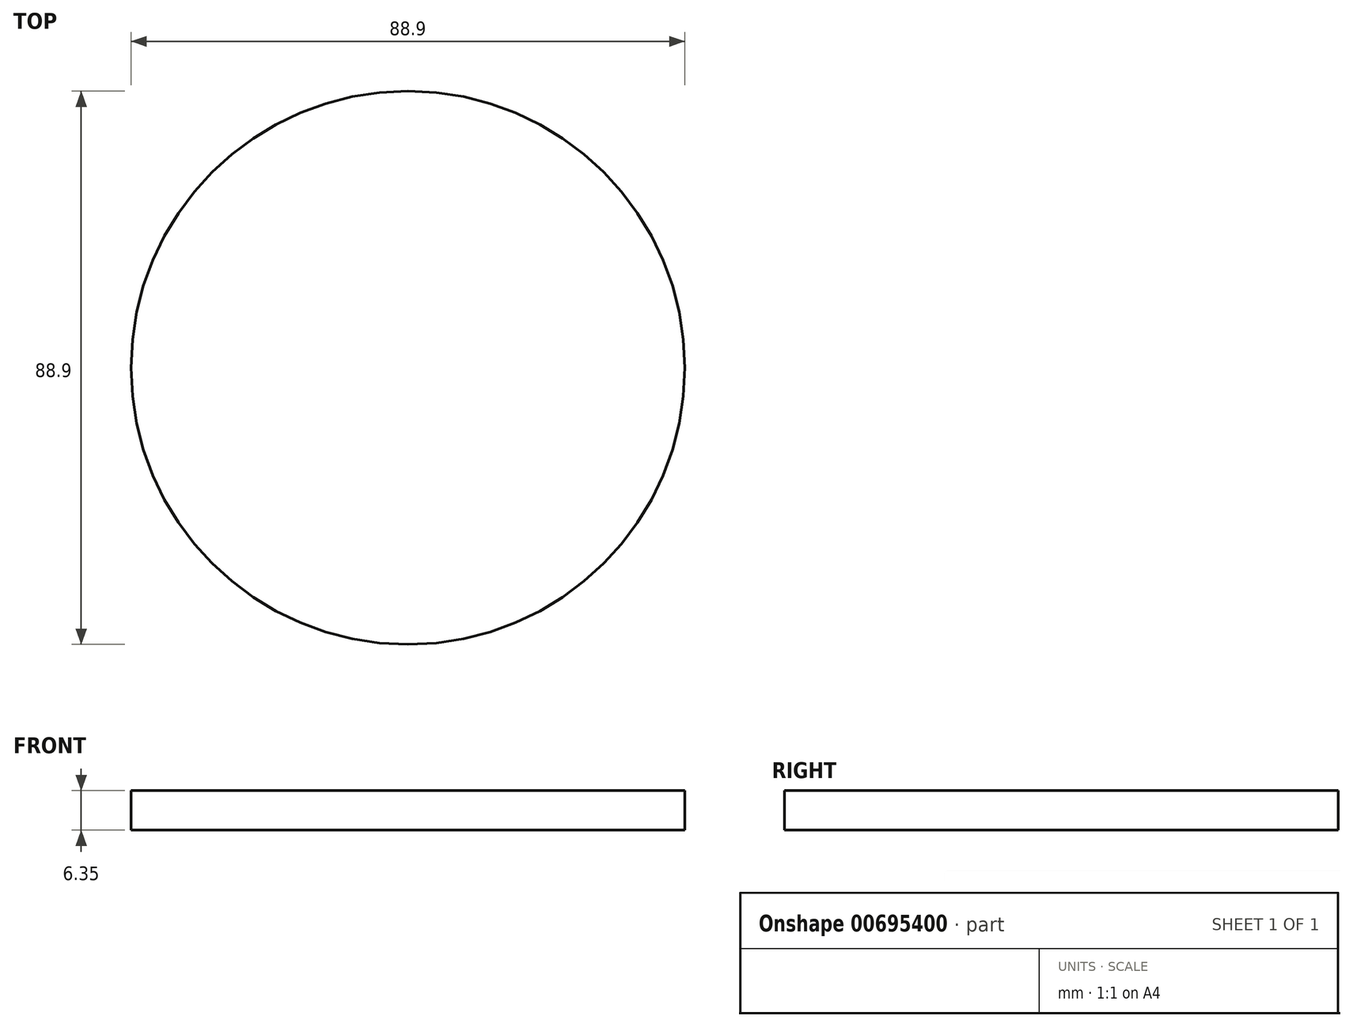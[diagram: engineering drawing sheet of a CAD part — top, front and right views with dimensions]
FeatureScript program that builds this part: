
annotation { "Feature Type Name" : "Feature", "Feature Type Description" : "" }
export const myFeature = defineFeature(function(context is Context, id is Id, definition is map)
    precondition{}
    {
        {
            var Q0;
            Q0=qCreatedBy(makeId("Top.planeOp"),FACE);
            var sketch = newSketch(context, id + "F0", { "sketchPlane" : qUnion([Q0])});
            skCircle(sketch, "E0", {"center": v(0, 0) * mm, "radius": 44.45 * mm});
            skSolve(sketch);
        }
        {
            var Q0;
            Q0 = qSketchRegion(id + "F0", true);
            extrude(context, id + "F1", {"entities" : qUnion([Q0]), "depth" : 6.35 * mm, "offsetDistance" : 25.4 * mm});
        }
    });
